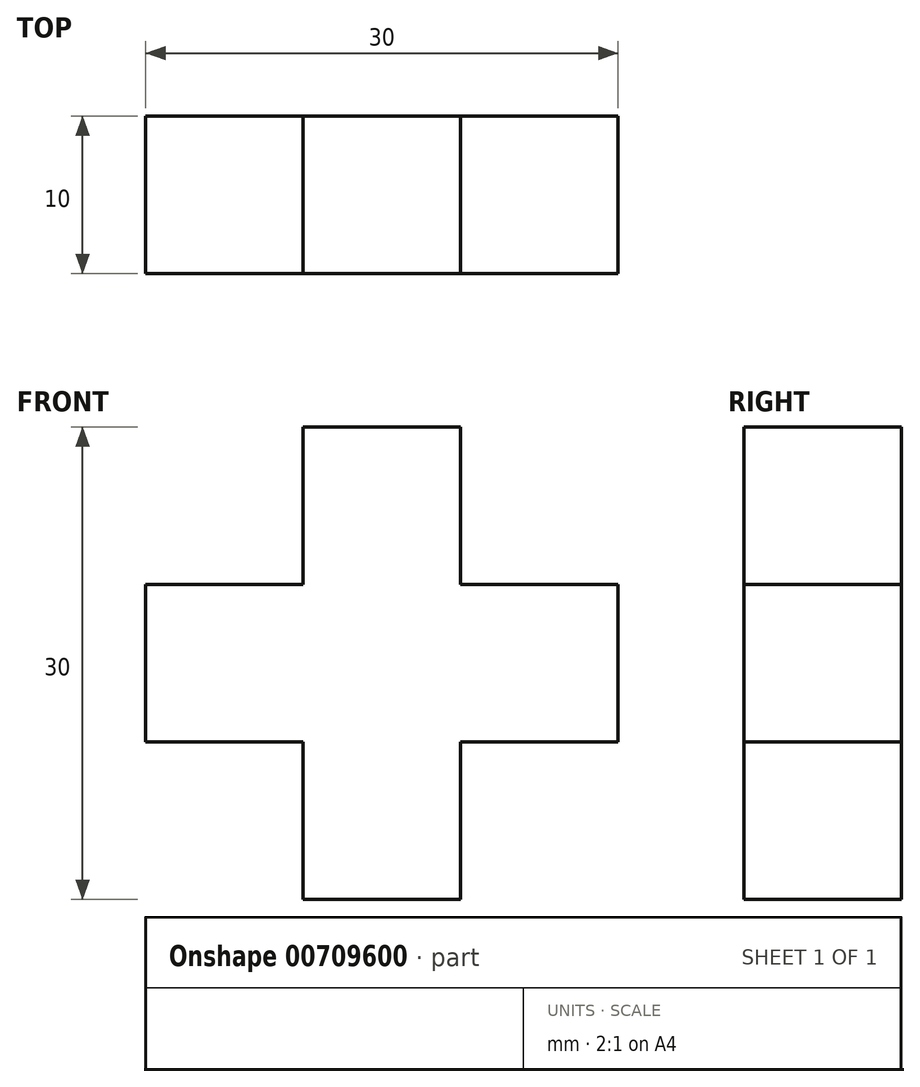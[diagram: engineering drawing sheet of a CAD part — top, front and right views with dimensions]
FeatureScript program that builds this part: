
annotation { "Feature Type Name" : "Feature", "Feature Type Description" : "" }
export const myFeature = defineFeature(function(context is Context, id is Id, definition is map)
    precondition{}
    {
        {
            var Q0;
            Q0=qCreatedBy(makeId("Front.planeOp"),FACE);
            var sketch = newSketch(context, id + "F0", { "sketchPlane" : qUnion([Q0])});
            skLineSegment(sketch, "E0.bottom", {"start": v(15, -5) * mm, "end": v(5, -5) * mm});
            skLineSegment(sketch, "E0.top", {"start": v(15, 5) * mm, "end": v(5, 5) * mm});
            skLineSegment(sketch, "E0.left", {"start": v(15, -5) * mm, "end": v(15, 5) * mm});
            skLineSegment(sketch, "E0.right", {"start": v(-15, -5) * mm, "end": v(-15, 5) * mm});
            skPoint(sketch, "E0.middle", {"position": v(0, 0) * mm});
            skLineSegment(sketch, "E1.bottom", {"start": v(5, -15) * mm, "end": v(-5, -15) * mm});
            skLineSegment(sketch, "E1.top", {"start": v(5, 15) * mm, "end": v(-5, 15) * mm});
            skLineSegment(sketch, "E1.left", {"start": v(5, -15) * mm, "end": v(5, -5) * mm});
            skLineSegment(sketch, "E1.right", {"start": v(-5, -15) * mm, "end": v(-5, -5) * mm});
            skLineSegment(sketch, "E2.trimOffspring", {"start": v(-5, 5) * mm, "end": v(-15, 5) * mm});
            skLineSegment(sketch, "E3.trimOffspring", {"start": v(-5, 5) * mm, "end": v(-5, 15) * mm});
            skLineSegment(sketch, "E4.trimOffspring", {"start": v(-5, -5) * mm, "end": v(-15, -5) * mm});
            skLineSegment(sketch, "E5.trimOffspring", {"start": v(5, 5) * mm, "end": v(5, 15) * mm});
            skSolve(sketch);
        }
        {
            var Q0;
            Q0=makeQuery(id+"F0.imprint","IMPRINT",FACE,{"disambiguationData":[TD([[makeQuery(id+"F0.imprint","IMPRINT",EDGE,{"derivedFrom":sQuery(id+"F0.wireOp",EDGE,"E0.bottom")}),-1.0]])]});
            extrude(context, id + "F1", {"entities" : qUnion([Q0]), "depth" : 10 * mm, "offsetDistance" : 25 * mm});
        }
    });
